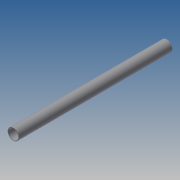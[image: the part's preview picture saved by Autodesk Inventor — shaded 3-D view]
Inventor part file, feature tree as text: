
AUTODESK INVENTOR PART (.ipt)
format: ipt  version: 2014 SP1 (Build 180222100, 222)  size: 70,656 bytes
history: native  units: in
note: dims shown in document units (in); Inventor stores cm internally (conversion verified against a paired STEP export)
features: extrude x1, sketch x1
ambient origin geometry x8: Origin, YZ Plane, XZ Plane, XY Plane, X Axis, Y Axis, Z Axis, Center Point
bodies: Solid1 (feature_tree)
feature tree (2):
  extrude  "Extrusion1"  Depth=59.0551in
  sketch  "Sketch1"  dims[d0=3.937in d1=0.2in d2=59.0551in d3=0.0in]
